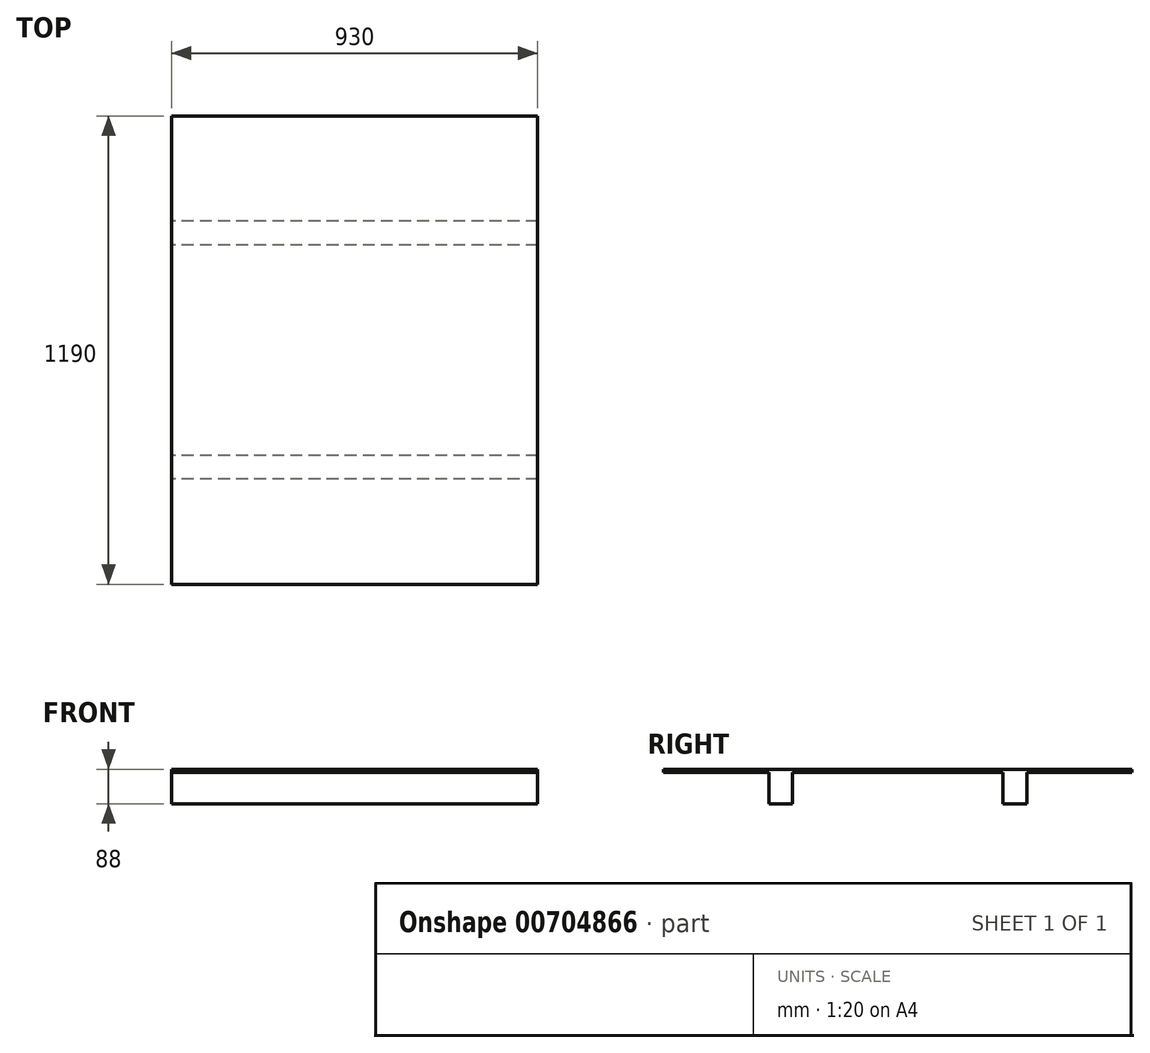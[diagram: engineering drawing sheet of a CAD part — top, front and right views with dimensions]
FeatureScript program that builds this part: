
annotation { "Feature Type Name" : "Feature", "Feature Type Description" : "" }
export const myFeature = defineFeature(function(context is Context, id is Id, definition is map)
    precondition{}
    {
        {
            var Q0;
            Q0=qCreatedBy(makeId("Top.planeOp"),FACE);
            var sketch = newSketch(context, id + "F0", { "sketchPlane" : qUnion([Q0])});
            skLineSegment(sketch, "E0.bottom", {"start": v(0, 0) * mm, "end": v(930, 0) * mm});
            skLineSegment(sketch, "E0.top", {"start": v(0, 1190) * mm, "end": v(930, 1190) * mm});
            skLineSegment(sketch, "E0.left", {"start": v(0, 0) * mm, "end": v(0, 1190) * mm});
            skLineSegment(sketch, "E0.right", {"start": v(930, 0) * mm, "end": v(930, 1190) * mm});
            skSolve(sketch);
        }
        {
            var Q0;
            Q0 = qSketchRegion(id + "F0", true);
            extrude(context, id + "F1", {"entities" : qUnion([Q0]), "depth" : 8 * mm, "offsetDistance" : 25 * mm});
        }
        {
            var Q0;
            Q0=makeQuery(id+"F1.opExtrude","CAP_FACE",FACE,{"disambiguationData":[OSD([sQuery(id+"F0.wireOp",EDGE,"E0.bottom"),sQuery(id+"F0.wireOp",EDGE,"E0.top"),sQuery(id+"F0.wireOp",EDGE,"E0.left"),sQuery(id+"F0.wireOp",EDGE,"E0.right")])],"isStart":true});
            var sketch = newSketch(context, id + "F2", { "sketchPlane" : qUnion([Q0])});
            skLineSegment(sketch, "E1", {"start": v(0, -595) * mm, "end": v(930, -595) * mm, "construction": true});
            skLineSegment(sketch, "E2.bottom", {"start": v(930, -267.5) * mm, "end": v(0, -267.5) * mm});
            skLineSegment(sketch, "E2.top", {"start": v(930, -327.5) * mm, "end": v(0, -327.5) * mm});
            skLineSegment(sketch, "E2.left", {"start": v(930, -267.5) * mm, "end": v(930, -327.5) * mm});
            skLineSegment(sketch, "E2.right", {"start": v(0, -267.5) * mm, "end": v(0, -327.5) * mm});
            skPoint(sketch, "E2.middle", {"position": v(465, -297.5) * mm});
            skPoint(sketch, "E2.middle.positionSnap0", {"position": v(465, -595) * mm});
            skPoint(sketch, "E2.centerSnap0", {"position": v(465, -595) * mm});
            skLineSegment(sketch, "E3.MirrorCS", {"start": v(930, -862.5) * mm, "end": v(0, -862.5) * mm});
            skLineSegment(sketch, "E4.MirrorCS", {"start": v(930, -922.5) * mm, "end": v(0, -922.5) * mm});
            skLineSegment(sketch, "E5.MirrorCS", {"start": v(0, -922.5) * mm, "end": v(0, -862.5) * mm});
            skLineSegment(sketch, "E6.MirrorCS", {"start": v(930, -922.5) * mm, "end": v(930, -862.5) * mm});
            skSolve(sketch);
        }
        {
            var Q0;
            Q0 = qSketchRegion(id + "F2", true);
            extrude(context, id + "F3", {"entities" : qUnion([Q0]), "operationType" : NewBodyOperationType.ADD, "depth" : 80 * mm, "offsetDistance" : 25 * mm});
        }
    });
